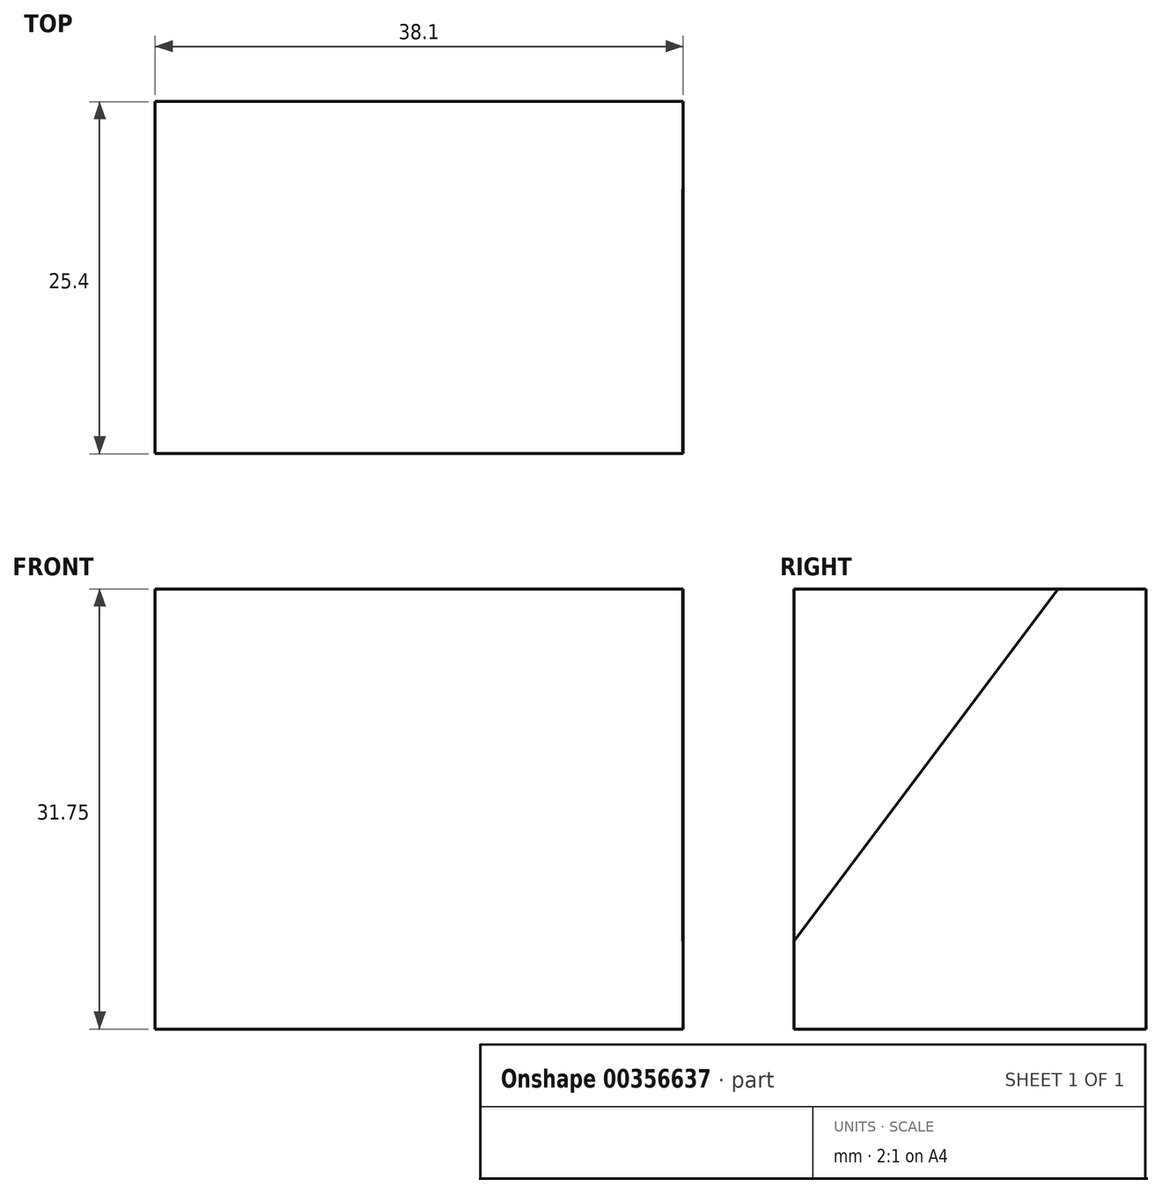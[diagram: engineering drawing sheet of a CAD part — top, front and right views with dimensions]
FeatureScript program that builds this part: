
annotation { "Feature Type Name" : "Feature", "Feature Type Description" : "" }
export const myFeature = defineFeature(function(context is Context, id is Id, definition is map)
    precondition{}
    {
        {
            var Q0;
            Q0=qCreatedBy(makeId("Right.planeOp"),FACE);
            var sketch = newSketch(context, id + "F0", { "sketchPlane" : qUnion([Q0])});
            skLineSegment(sketch, "E0", {"start": v(43.93, 31.75) * mm, "end": v(43.93, 0) * mm});
            skLineSegment(sketch, "E1", {"start": v(43.93, 0) * mm, "end": v(18.53, 0) * mm});
            skLineSegment(sketch, "E2", {"start": v(18.53, 0) * mm, "end": v(18.53, 31.75) * mm});
            skLineSegment(sketch, "E3", {"start": v(18.53, 31.75) * mm, "end": v(43.93, 31.75) * mm});
            skSolve(sketch);
        }
        {
            var Q0;
            Q0 = qSketchRegion(id + "F0", true);
            extrude(context, id + "F1", {"entities" : qUnion([Q0]), "depth" : 38.1 * mm});
        }
        {
            var Q0;
            Q0=qCreatedBy(makeId("Right.planeOp"),FACE);
            var sketch = newSketch(context, id + "F2", { "sketchPlane" : qUnion([Q0])});
            skLineSegment(sketch, "E4", {"start": v(24.73, 31.56) * mm, "end": v(44.09, 6.16) * mm});
            skLineSegment(sketch, "E5", {"start": v(24.73, 31.56) * mm, "end": v(43.78, 31.56) * mm});
            skLineSegment(sketch, "E6", {"start": v(43.78, 31.56) * mm, "end": v(44.09, 6.16) * mm});
            skSolve(sketch);
        }
        {
            var Q0;
            Q0=makeQuery(id+"F2.imprint","IMPRINT",FACE,{"disambiguationData":[TD([[makeQuery(id+"F2.imprint","IMPRINT",EDGE,{"derivedFrom":sQuery(id+"F2.wireOp",EDGE,"E4")}),1.0]])]});
            extrude(context, id + "F3", {"entities" : qUnion([Q0]), "operationType" : NewBodyOperationType.REMOVE, "oppositeDirection" : true, "depth" : 25.4 * mm});
        }
        {
            var Q0;
            Q0 = qSketchRegion(id + "F2", true);
            extrude(context, id + "F4", {"entities" : qUnion([Q0]), "operationType" : NewBodyOperationType.REMOVE, "oppositeDirection" : true, "depth" : 25.4 * mm});
        }
        {
            var Q0;
            Q0=makeQuery(id+"F1.opExtrude","CAP_FACE",FACE,{"disambiguationData":[OSD([sQuery(id+"F0.wireOp",EDGE,"E0"),sQuery(id+"F0.wireOp",EDGE,"E1"),sQuery(id+"F0.wireOp",EDGE,"E2"),sQuery(id+"F0.wireOp",EDGE,"E3")])],"isStart":false});
            var sketch = newSketch(context, id + "F5", { "sketchPlane" : qUnion([Q0])});
            skLineSegment(sketch, "E7", {"start": v(37.58, 31.75) * mm, "end": v(18.53, 6.35) * mm});
            skSolve(sketch);
        }
        {
            var Q0;
            {var subQ0=sQuery(id+"F5.wireOp",EDGE,"E7");Q0=makeQuery(id+"F5.imprint","IMPRINT",FACE,{"disambiguationData":[TD([[makeQuery(id+"F5.imprint","IMPRINT",EDGE,{"derivedFrom":subQ0}),-1.0]])]});}
            extrude(context, id + "F6", {"entities" : qUnion([Q0]), "operationType" : NewBodyOperationType.REMOVE, "oppositeDirection" : true, "depth" : 4 / 152.4 * mm});
        }
    });
